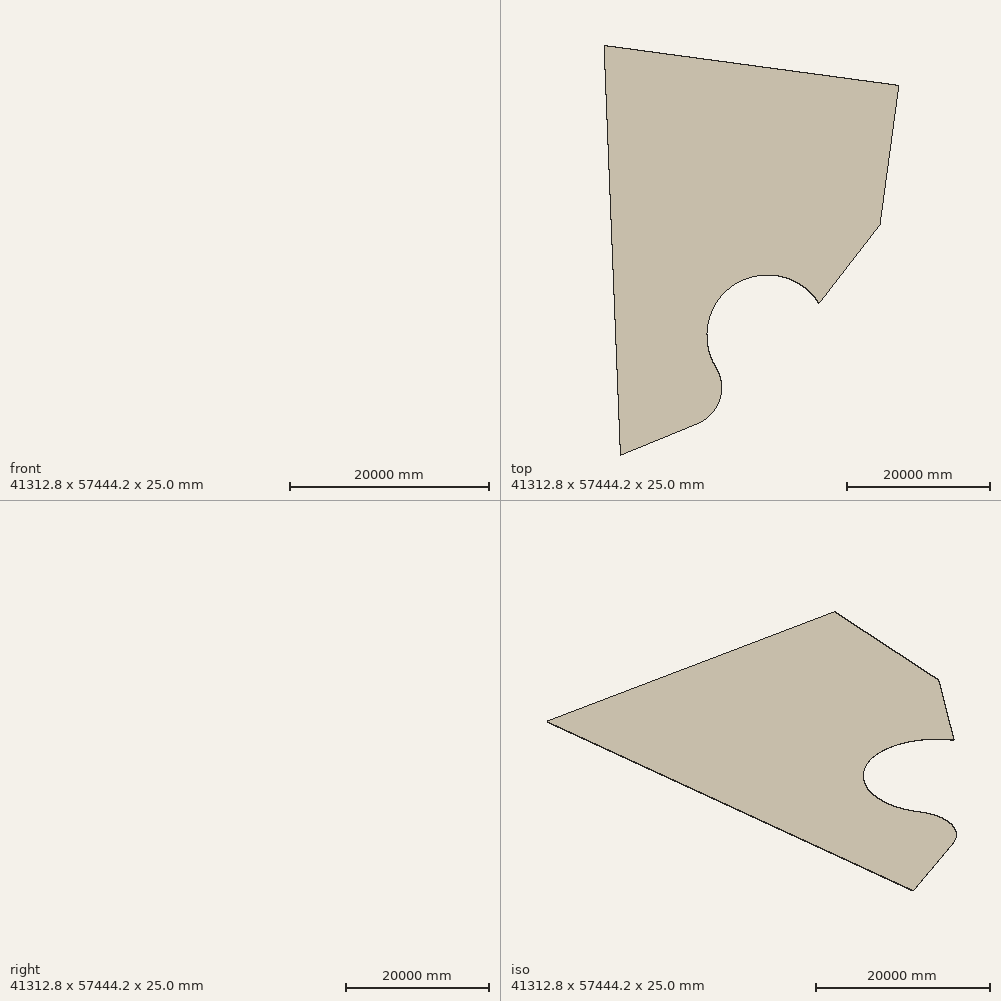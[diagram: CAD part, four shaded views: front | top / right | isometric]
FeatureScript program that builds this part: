
annotation { "Feature Type Name" : "Feature", "Feature Type Description" : "" }
export const myFeature = defineFeature(function(context is Context, id is Id, definition is map)
    precondition{}
    {
        {
            var Q0;
            Q0=qCreatedBy(makeId("Top.planeOp"),FACE);
            var sketch = newSketch(context, id + "F0", { "sketchPlane" : qUnion([Q0])});
            skLineSegment(sketch, "E0", {"start": v(0, 0) * mm, "end": v(8515.08, 11011.8) * mm});
            skLineSegment(sketch, "E1", {"start": v(8515.08, 11011.8) * mm, "end": v(11167.3, 30593) * mm});
            skLineSegment(sketch, "E2", {"start": v(11167.3, 30593) * mm, "end": v(-30145.45, 36188.72) * mm});
            skLineSegment(sketch, "E3", {"start": v(-30145.45, 36188.72) * mm, "end": v(-27851.95, -21255.51) * mm});
            skLineSegment(sketch, "E4", {"start": v(-27851.95, -21255.51) * mm, "end": v(-17025.94, -16818.45) * mm});
            skArc(sketch, "E5", {"start": v(-17025.94, -16818.45) * mm, "mid": v(-13918.48, -13469.67) * mm, "end": v(-14463.28, -8933.84) * mm});
            skArc(sketch, "E6", {"start": v(0, 0) * mm, "mid": v(-11698.56, 2764.72) * mm, "end": v(-14463.28, -8933.84) * mm});
            skLineSegment(sketch, "E7", {"start": v(0, 0) * mm, "end": v(-14463.28, -8933.84) * mm, "construction": true});
            skSolve(sketch);
        }
        {
            var Q0;
            Q0 = qSketchRegion(id + "F0", true);
            extrude(context, id + "F1", {"entities" : qUnion([Q0]), "depth" : 25 * mm, "offsetDistance" : 25 * mm});
        }
    });
